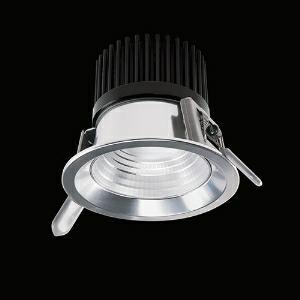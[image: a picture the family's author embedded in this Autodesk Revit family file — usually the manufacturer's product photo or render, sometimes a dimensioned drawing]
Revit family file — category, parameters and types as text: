
# Revit family: spectral_myral_myral_3500-830-s
name_source: partatom
category: Lighting Fixtures
revit_build: Autodesk Revit 2016 (Build: 20150220_1215(x64)
units: mm (PartAtom-declared; Revit-internal decimal feet)

## family parameters
Cut with Voids When Loaded = No
Host = Face
Light Source = No
Part Type = Normal
Room Calculation Point = No
Round Connector Dimension = Use Diameter
Shared = No

## types (1)
- SPECTRAL MYRAL (1 x )
    Apparent Load = 0 VA
    Approval mark = CE
    CIE Flux Codes = 85 100 100 100 100
    Control Gear = Electronic transformer
    Default Elevation = 1800 mm
    Description = SPG0320174
MYRAL recessed spot

Design:
    Height = 0 mm  [stored 0 ft]
    Lamp = 1 x
    Lamp count = 1
    Length = 120 mm
    Luminous efficacy = 0 lm/W
    Manufacturer = Ridi
    ModVariant = No
    Model = MYRAL 3500-830-S
    Mounting Place = Ceiling
    Mounting Type = Recessed
    Number of Poles = 1
    OnlyDefault = Yes
    Power Factor = 1
    Product Name = SPECTRAL MYRAL
    Product group = Downlight recessed
    ProductGroupID = 400
    Protection Class = Protection class
    Protection Degree = IP 20
    RlxData = <blob elided: 38913 chars, md5=60f9e85f>
    Socket = socket
    Standby Power = 0 W
    System Light Flux = 0 lm
    System Power = 0 W
    Type Image = myral_04.jpg
    URL = http://reluxnet.relux.com
    VarID = ---
    Voltage = 0 V
    Weight = 0.00 kg
    Width = 0 mm  [stored 0 ft]

note: [stored X ft] marks values corroborated as IEEE doubles in the binary element streams (Revit-internal decimal feet)

## geometry (parser evidence)
native form markers: Sweep x10
no freeform markers — native parametric forms only
